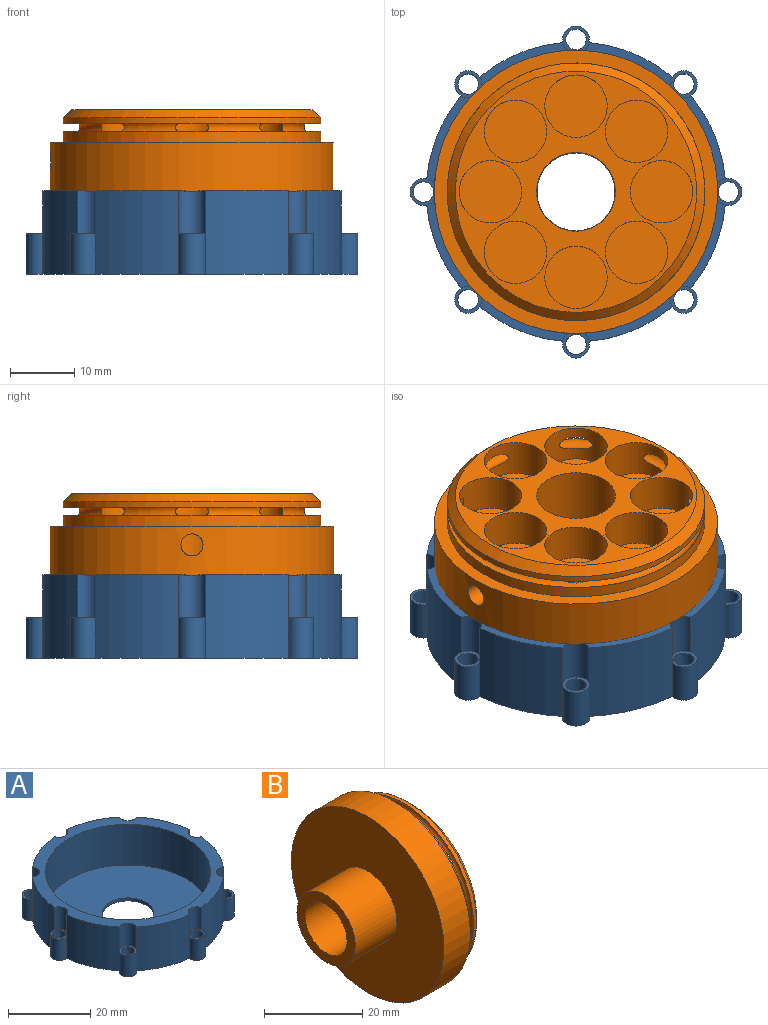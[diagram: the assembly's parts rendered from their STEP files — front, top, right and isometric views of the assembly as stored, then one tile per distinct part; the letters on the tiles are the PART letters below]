
ASSEMBLY  parts=2 mates=1
PART A: 45 faces, bbox 51.5x51.5x13 mm
  f0: cylinder r=23.27mm len=13mm, axis (0,0,-1), area 184.3mm2, adj f8,f11,f12,f13,f14,f25,f36,f43
  f1: cylinder r=23.27mm len=13mm, axis (0,0,-1), area 184.3mm2, adj f8,f13,f14,f15,f16,f25,f42,f43
  f2: cylinder r=23.27mm len=13mm, axis (0,0,-1), area 184.3mm2, adj f8,f15,f16,f17,f18,f25,f41,f42
  f3: cylinder r=23.27mm len=13mm, axis (0,0,-1), area 184.3mm2, adj f8,f17,f18,f19,f20,f25,f40,f41
  f4: cylinder r=23.27mm len=13mm, axis (0,0,-1), area 184.3mm2, adj f8,f19,f20,f21,f22,f25,f39,f40
  f5: cylinder r=23.27mm len=13mm, axis (0,0,-1), area 184.3mm2, adj f8,f21,f22,f23,f24,f25,f38,f39
  f6: cylinder r=23.27mm len=13mm, axis (0,0,-1), area 184.3mm2, adj f8,f23,f24,f25,f26,f27,f37,f38
  f7: cylinder r=23.27mm len=13mm, axis (0,0,-1), area 184.3mm2, adj f8,f11,f12,f25,f26,f27,f36,f37
  f8: plane 46.35x46.35mm, normal (0,0,1), area 390.1mm2, adj f0,f1,f2,f3,f4,f5,f6,f7
  f9: cylinder r=20.1mm len=40.2mm, axis (0,0,1), area 1528.1mm2, adj f8,f10
  f10: plane 40.2x40.2mm, normal (0,0,1), area 1146.5mm2, adj f9,f44
  f11: plane 4.21x4.2mm, normal (0,0,1), area 6mm2, adj f0,f7,f12,f28,f36
  f12: cylinder r=2.1mm len=6.35mm, axis (0,0,-1), area 48.3mm2, adj f0,f7,f11,f25
  f13: plane 4.21x4.21mm, normal (0,0,1), area 6mm2, adj f0,f1,f14,f35,f43
  f14: cylinder r=2.1mm len=6.35mm, axis (0,0,-1), area 48.3mm2, adj f0,f1,f13,f25
  f15: plane 4.21x4.2mm, normal (0,0,1), area 6mm2, adj f1,f2,f16,f34,f42
  f16: cylinder r=2.1mm len=6.35mm, axis (0,0,-1), area 48.3mm2, adj f1,f2,f15,f25
  f17: plane 4.21x4.21mm, normal (0,0,1), area 6mm2, adj f2,f3,f18,f33,f41
  f18: cylinder r=2.1mm len=6.35mm, axis (0,0,-1), area 48.3mm2, adj f2,f3,f17,f25
  f19: plane 4.21x4.2mm, normal (0,0,1), area 6mm2, adj f3,f4,f20,f32,f40
  f20: cylinder r=2.1mm len=6.35mm, axis (0,0,-1), area 48.3mm2, adj f3,f4,f19,f25
  f21: plane 4.21x4.21mm, normal (0,0,1), area 6mm2, adj f4,f5,f22,f31,f39
  f22: cylinder r=2.1mm len=6.35mm, axis (0,0,-1), area 48.3mm2, adj f4,f5,f21,f25
  f23: plane 4.21x4.2mm, normal (0,0,1), area 6mm2, adj f5,f6,f24,f30,f38
  f24: cylinder r=2.1mm len=6.35mm, axis (0,0,-1), area 48.3mm2, adj f5,f6,f23,f25
  f25: plane 51.55x51.55mm, normal (0,0,-1), area 1584.6mm2, adj f0,f1,f2,f3,f4,f5,f6,f7
  f26: plane 4.21x4.21mm, normal (0,0,1), area 6mm2, adj f6,f7,f27,f29,f37
  f27: cylinder r=2.1mm len=6.35mm, axis (0,0,-1), area 48.3mm2, adj f6,f7,f25,f26
  f28: cylinder r=1.59mm len=6.35mm, axis (0,0,1), area 63.3mm2, adj f11,f25
  f29: cylinder r=1.59mm len=6.35mm, axis (0,0,1), area 63.3mm2, adj f25,f26
  f30: cylinder r=1.59mm len=6.35mm, axis (0,0,1), area 63.3mm2, adj f23,f25
  f31: cylinder r=1.59mm len=6.35mm, axis (0,0,1), area 63.3mm2, adj f21,f25
  f32: cylinder r=1.59mm len=6.35mm, axis (0,0,1), area 63.3mm2, adj f19,f25
  f33: cylinder r=1.59mm len=6.35mm, axis (0,0,1), area 63.3mm2, adj f17,f25
  f34: cylinder r=1.59mm len=6.35mm, axis (0,0,1), area 63.3mm2, adj f15,f25
  f35: cylinder r=1.59mm len=6.35mm, axis (0,0,1), area 63.3mm2, adj f13,f25
  f36: cylinder r=2.11mm len=6.65mm, axis (0,0,-1), area 37.4mm2, adj f0,f7,f8,f11
  f37: cylinder r=2.11mm len=6.65mm, axis (0,0,-1), area 37.4mm2, adj f6,f7,f8,f26
  f38: cylinder r=2.11mm len=6.65mm, axis (0,0,-1), area 37.4mm2, adj f5,f6,f8,f23
  f39: cylinder r=2.11mm len=6.65mm, axis (0,0,-1), area 37.4mm2, adj f4,f5,f8,f21
  f40: cylinder r=2.11mm len=6.65mm, axis (0,0,-1), area 37.4mm2, adj f3,f4,f8,f19
  f41: cylinder r=2.11mm len=6.65mm, axis (0,0,-1), area 37.4mm2, adj f2,f3,f8,f17
  f42: cylinder r=2.11mm len=6.65mm, axis (0,0,-1), area 37.4mm2, adj f1,f2,f8,f15
  f43: cylinder r=2.11mm len=6.65mm, axis (0,0,-1), area 37.4mm2, adj f0,f1,f8,f13
  f44: cylinder r=6.25mm len=12.5mm, axis (0,0,1), area 35.3mm2, adj f10,f25
PART B: 30 faces, bbox 24.7x44x44 mm
  f0: cylinder r=4.85mm len=9.7mm, axis (1,0,0), area 168.9mm2, adj f11,f19,f28
  f1: cylinder r=4.85mm len=9.7mm, axis (1,0,0), area 168.9mm2, adj f11,f20,f28
  f2: cylinder r=4.85mm len=9.7mm, axis (1,0,0), area 169mm2, adj f11,f21,f28
  f3: cylinder r=4.85mm len=9.7mm, axis (1,0,0), area 168.9mm2, adj f11,f22,f28
  f4: cylinder r=4.85mm len=9.7mm, axis (1,0,0), area 168.9mm2, adj f11,f23,f28
  f5: cylinder r=4.85mm len=9.7mm, axis (1,0,0), area 168.9mm2, adj f11,f24,f28
  f6: cylinder r=4.85mm len=9.7mm, axis (1,0,0), area 169mm2, adj f11,f25,f28
  f7: cylinder r=4.85mm len=9.7mm, axis (1,0,0), area 168.9mm2, adj f11,f26,f28
  f8: cylinder r=20mm len=40mm, axis (1,0,0), area 115.1mm2, adj f28,f29
  f9: cylinder r=20mm len=40mm, axis (1,0,0), area 219.6mm2, adj f27,f28
  f10: cylinder r=22mm len=44mm, axis (-1,0,0), area 1044.1mm2, adj f13,f14,f27
  f11: plane 37.46x37.46mm, normal (1,0,0), area 393.1mm2, adj f0,f1,f2,f3,f4,f5,f6,f7
  f12: cylinder r=6.12mm len=12.7mm, axis (1,0,0), area 479.4mm2, adj f11,f13,f15
  f13: cylinder r=1.71mm len=16.12mm, axis (0,0,1), area 172mm2, adj f10,f12
  f14: plane 44x44mm, normal (-1,0,0), area 1298.9mm2, adj f10,f16
  f15: plane 12.25x12.25mm, normal (1,0,0), area 2.9mm2, adj f12,f17
  f16: cylinder r=8.4mm len=16.8mm, axis (1,0,0), area 633.3mm2, adj f14,f18
  f17: cylinder r=6.05mm len=12.1mm, axis (1,0,0), area 456.2mm2, adj f15,f18
  f18: plane 16.8x16.8mm, normal (-1,0,0), area 106.7mm2, adj f16,f17
  f19: plane 9.7x9.7mm, normal (1,0,0), area 73.9mm2, adj f0
  f20: plane 9.7x9.7mm, normal (1,0,0), area 73.9mm2, adj f1
  f21: plane 9.7x9.7mm, normal (1,0,0), area 73.9mm2, adj f2
  f22: plane 9.7x9.7mm, normal (1,0,0), area 73.9mm2, adj f3
  f23: plane 9.7x9.7mm, normal (1,0,0), area 73.9mm2, adj f4
  f24: plane 9.7x9.7mm, normal (1,0,0), area 73.9mm2, adj f5
  f25: plane 9.7x9.7mm, normal (1,0,0), area 73.9mm2, adj f6
  f26: plane 9.7x9.7mm, normal (1,0,0), area 73.9mm2, adj f7
  f27: plane 44x44mm, normal (1,0,0), area 263.9mm2, adj f9,f10
  f28: torus R=18.87mm, axis (1,0,0), area 717.2mm2, adj f0,f1,f2,f3,f4,f5,f6,f7
  f29: cone r=18.73mm half-angle=45deg, axis (-1,0,0), area 218.5mm2, adj f8,f11
PLACE A t=(73.1,38.79,-11.61)mm
PLACE B rot(axis=(0.71,0,0.71),180deg) t=(73.1,38.79,1.29)mm
MATE slider B.f17 <-> A.f9  axis (0,0,-1) through (73.1,38.79,-10.71)mm
